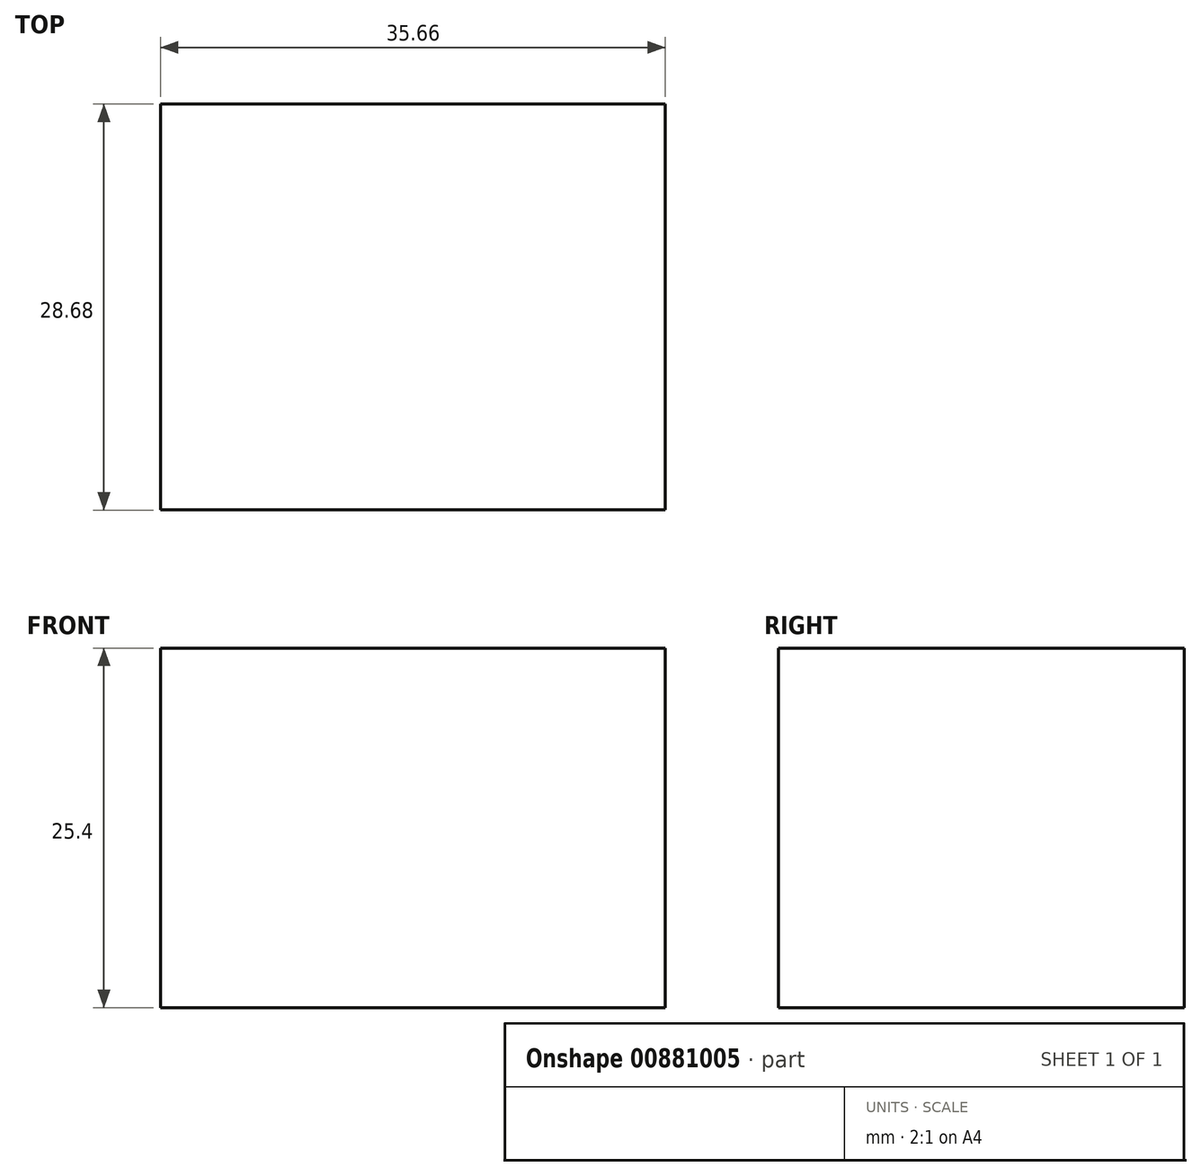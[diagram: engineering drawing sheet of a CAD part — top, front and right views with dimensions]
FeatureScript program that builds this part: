
annotation { "Feature Type Name" : "Feature", "Feature Type Description" : "" }
export const myFeature = defineFeature(function(context is Context, id is Id, definition is map)
    precondition{}
    {
        {
            var Q0;
            Q0=qCreatedBy(makeId("Top.planeOp"),FACE);
            var sketch = newSketch(context, id + "F0", { "sketchPlane" : qUnion([Q0])});
            skLineSegment(sketch, "E0.bottom", {"start": v(-44.7, 33.86) * mm, "end": v(-9.04, 33.86) * mm});
            skLineSegment(sketch, "E0.top", {"start": v(-44.7, 5.18) * mm, "end": v(-9.04, 5.18) * mm});
            skLineSegment(sketch, "E0.left", {"start": v(-44.7, 33.86) * mm, "end": v(-44.7, 5.18) * mm});
            skLineSegment(sketch, "E0.right", {"start": v(-9.04, 33.86) * mm, "end": v(-9.04, 5.18) * mm});
            skSolve(sketch);
        }
        {
            var Q0;
            Q0 = qSketchRegion(id + "F0", true);
            extrude(context, id + "F1", {"entities" : qUnion([Q0]), "depth" : 25.4 * mm, "offsetDistance" : 25.4 * mm});
        }
    });
